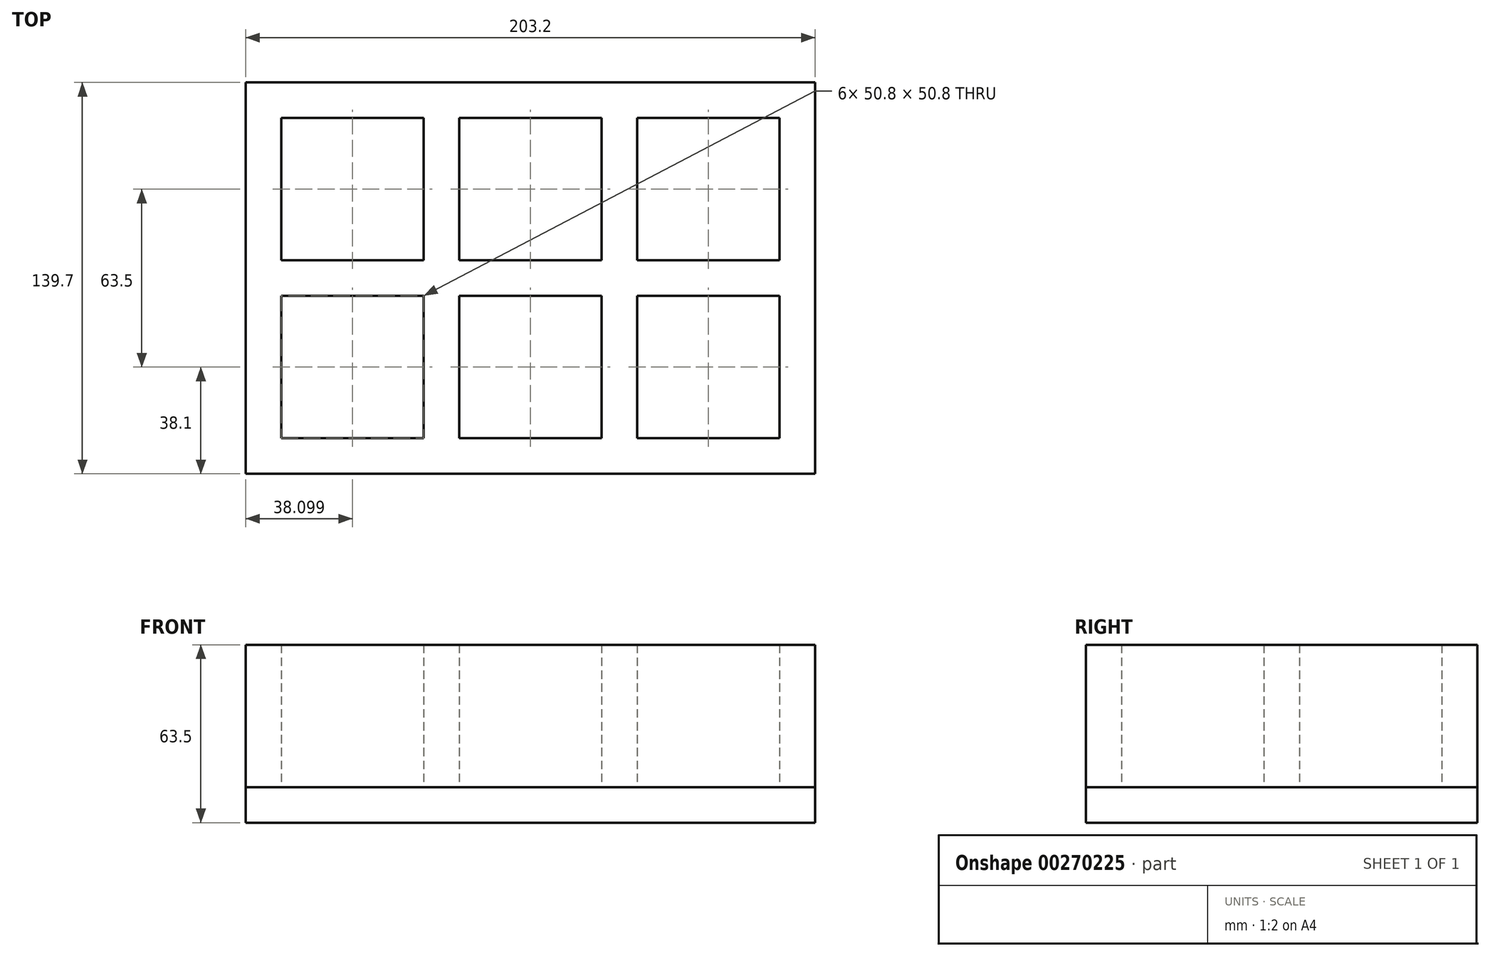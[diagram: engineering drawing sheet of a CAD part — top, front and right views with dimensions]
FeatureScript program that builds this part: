
annotation { "Feature Type Name" : "Feature", "Feature Type Description" : "" }
export const myFeature = defineFeature(function(context is Context, id is Id, definition is map)
    precondition{}
    {
        {
            var Q0;
            Q0=qCreatedBy(makeId("Top.planeOp"),FACE);
            var sketch = newSketch(context, id + "F0", { "sketchPlane" : qUnion([Q0])});
            skLineSegment(sketch, "E0.bottom", {"start": v(-73.54, -55.31) * mm, "end": v(104.26, -55.31) * mm});
            skLineSegment(sketch, "E0.top", {"start": v(-73.54, 58.99) * mm, "end": v(104.26, 58.99) * mm});
            skLineSegment(sketch, "E0.left", {"start": v(-73.54, -55.31) * mm, "end": v(-73.54, 58.99) * mm});
            skLineSegment(sketch, "E0.right", {"start": v(104.26, -55.31) * mm, "end": v(104.26, 58.99) * mm});
            skLineSegment(sketch, "E1", {"start": v(-10.04, 58.99) * mm, "end": v(-10.04, -55.31) * mm});
            skLineSegment(sketch, "E2", {"start": v(53.46, 58.99) * mm, "end": v(53.46, -55.31) * mm});
            skLineSegment(sketch, "E3", {"start": v(-22.74, 58.99) * mm, "end": v(-22.74, -55.31) * mm});
            skLineSegment(sketch, "E4", {"start": v(40.76, 58.99) * mm, "end": v(40.76, -55.31) * mm});
            skLineSegment(sketch, "E5", {"start": v(-73.54, 8.19) * mm, "end": v(104.26, 8.19) * mm});
            skLineSegment(sketch, "E6", {"start": v(-73.54, -4.51) * mm, "end": v(104.26, -4.51) * mm});
            skLineSegment(sketch, "E7.bottom", {"start": v(-86.24, 71.69) * mm, "end": v(116.96, 71.69) * mm});
            skLineSegment(sketch, "E7.top", {"start": v(-86.24, -68.01) * mm, "end": v(116.96, -68.01) * mm});
            skLineSegment(sketch, "E7.left", {"start": v(-86.24, 71.69) * mm, "end": v(-86.24, -68.01) * mm});
            skLineSegment(sketch, "E7.right", {"start": v(116.96, 71.69) * mm, "end": v(116.96, -68.01) * mm});
            skSolve(sketch);
        }
        {
            var Q0;
            Q0=makeQuery(id+"F0.imprint","IMPRINT",FACE,{"disambiguationData":[TD([[makeQuery(id+"F0.imprint","IMPRINT",EDGE,{"derivedFrom":sQuery(id+"F0.wireOp",EDGE,"E7.bottom")}),-1.0]])]});
            var Q1;
            {var subQ0=sQuery(id+"F0.wireOp",EDGE,"E5");var subQ1=sQuery(id+"F0.wireOp",EDGE,"E0.left");var subQ2=makeQuery(id+"F0.imprint","INTERSECT",VERTEX,{"derivedFrom":[subQ1,subQ0]});Q1=makeQuery(id+"F0.imprint","IMPRINT",FACE,{"disambiguationData":[TD([[makeQuery(id+"F0.imprint","IMPRINT",EDGE,{"disambiguationData":[TD([[subQ2,1.0]])],"derivedFrom":subQ1}),-1.0]])]});}
            var Q2;
            {var subQ0=sQuery(id+"F0.wireOp",EDGE,"E5");var subQ1=sQuery(id+"F0.wireOp",EDGE,"E1");var subQ2=makeQuery(id+"F0.imprint","INTERSECT",VERTEX,{"derivedFrom":[subQ1,subQ0]});Q2=makeQuery(id+"F0.imprint","IMPRINT",FACE,{"disambiguationData":[TD([[makeQuery(id+"F0.imprint","IMPRINT",EDGE,{"disambiguationData":[TD([[subQ2,-1.0]])],"derivedFrom":subQ1}),1.0]])]});}
            var Q3;
            {var subQ0=sQuery(id+"F0.wireOp",EDGE,"E5");var subQ1=sQuery(id+"F0.wireOp",EDGE,"E1");var subQ2=makeQuery(id+"F0.imprint","INTERSECT",VERTEX,{"derivedFrom":[subQ1,subQ0]});Q3=makeQuery(id+"F0.imprint","IMPRINT",FACE,{"disambiguationData":[TD([[makeQuery(id+"F0.imprint","IMPRINT",EDGE,{"disambiguationData":[TD([[subQ2,-1.0]])],"derivedFrom":subQ1}),-1.0]])]});}
            var Q4;
            {var subQ0=sQuery(id+"F0.wireOp",EDGE,"E5");var subQ1=sQuery(id+"F0.wireOp",EDGE,"E2");var subQ2=makeQuery(id+"F0.imprint","INTERSECT",VERTEX,{"derivedFrom":[subQ1,subQ0]});Q4=makeQuery(id+"F0.imprint","IMPRINT",FACE,{"disambiguationData":[TD([[makeQuery(id+"F0.imprint","IMPRINT",EDGE,{"disambiguationData":[TD([[subQ2,-1.0]])],"derivedFrom":subQ1}),-1.0]])]});}
            var Q5;
            {var subQ0=sQuery(id+"F0.wireOp",EDGE,"E5");var subQ1=sQuery(id+"F0.wireOp",EDGE,"E0.right");var subQ2=makeQuery(id+"F0.imprint","INTERSECT",VERTEX,{"derivedFrom":[subQ1,subQ0]});Q5=makeQuery(id+"F0.imprint","IMPRINT",FACE,{"disambiguationData":[TD([[makeQuery(id+"F0.imprint","IMPRINT",EDGE,{"disambiguationData":[TD([[subQ2,1.0]])],"derivedFrom":subQ1}),1.0]])]});}
            var Q6;
            {var subQ0=sQuery(id+"F0.wireOp",EDGE,"E2");var subQ1=sQuery(id+"F0.wireOp",EDGE,"E0.bottom");var subQ2=makeQuery(id+"F0.imprint","INTERSECT",VERTEX,{"derivedFrom":[subQ1,subQ0]});Q6=makeQuery(id+"F0.imprint","IMPRINT",FACE,{"disambiguationData":[TD([[makeQuery(id+"F0.imprint","IMPRINT",EDGE,{"disambiguationData":[TD([[subQ2,1.0]])],"derivedFrom":subQ1}),1.0]])]});}
            var Q7;
            {var subQ0=sQuery(id+"F0.wireOp",EDGE,"E1");var subQ1=sQuery(id+"F0.wireOp",EDGE,"E0.bottom");var subQ2=makeQuery(id+"F0.imprint","INTERSECT",VERTEX,{"derivedFrom":[subQ1,subQ0]});Q7=makeQuery(id+"F0.imprint","IMPRINT",FACE,{"disambiguationData":[TD([[makeQuery(id+"F0.imprint","IMPRINT",EDGE,{"disambiguationData":[TD([[subQ2,1.0]])],"derivedFrom":subQ1}),1.0]])]});}
            var Q8;
            {var subQ0=sQuery(id+"F0.wireOp",EDGE,"E2");var subQ1=sQuery(id+"F0.wireOp",EDGE,"E0.top");var subQ2=makeQuery(id+"F0.imprint","INTERSECT",VERTEX,{"derivedFrom":[subQ1,subQ0]});Q8=makeQuery(id+"F0.imprint","IMPRINT",FACE,{"disambiguationData":[TD([[makeQuery(id+"F0.imprint","IMPRINT",EDGE,{"disambiguationData":[TD([[subQ2,1.0]])],"derivedFrom":subQ1}),-1.0]])]});}
            var Q9;
            {var subQ0=sQuery(id+"F0.wireOp",EDGE,"E1");var subQ1=sQuery(id+"F0.wireOp",EDGE,"E0.top");var subQ2=makeQuery(id+"F0.imprint","INTERSECT",VERTEX,{"derivedFrom":[subQ1,subQ0]});Q9=makeQuery(id+"F0.imprint","IMPRINT",FACE,{"disambiguationData":[TD([[makeQuery(id+"F0.imprint","IMPRINT",EDGE,{"disambiguationData":[TD([[subQ2,1.0]])],"derivedFrom":subQ1}),-1.0]])]});}
            extrude(context, id + "F1", {"entities" : qUnion([Q0, Q1, Q2, Q3, Q4, Q5, Q6, Q7, Q8, Q9]), "depth" : 50.8 * mm});
        }
        {
            var Q0;
            {var subQ0=sQuery(id+"F0.wireOp",EDGE,"E0.right");var subQ1=sQuery(id+"F0.wireOp",EDGE,"E0.top");var subQ2=makeQuery(id+"F0.imprint","INTERSECT",VERTEX,{"derivedFrom":[subQ1,subQ0]});Q0=makeQuery(id+"F0.imprint","IMPRINT",FACE,{"disambiguationData":[TD([[makeQuery(id+"F0.imprint","IMPRINT",EDGE,{"disambiguationData":[TD([[subQ2,1.0]])],"derivedFrom":subQ1}),-1.0]])]});}
            var Q1;
            {var subQ0=sQuery(id+"F0.wireOp",EDGE,"E5");var subQ1=sQuery(id+"F0.wireOp",EDGE,"E0.right");var subQ2=makeQuery(id+"F0.imprint","INTERSECT",VERTEX,{"derivedFrom":[subQ1,subQ0]});Q1=makeQuery(id+"F0.imprint","IMPRINT",FACE,{"disambiguationData":[TD([[makeQuery(id+"F0.imprint","IMPRINT",EDGE,{"disambiguationData":[TD([[subQ2,1.0]])],"derivedFrom":subQ1}),1.0]])]});}
            var Q2;
            {var subQ0=sQuery(id+"F0.wireOp",EDGE,"E0.right");var subQ1=sQuery(id+"F0.wireOp",EDGE,"E0.bottom");var subQ2=makeQuery(id+"F0.imprint","INTERSECT",VERTEX,{"derivedFrom":[subQ1,subQ0]});Q2=makeQuery(id+"F0.imprint","IMPRINT",FACE,{"disambiguationData":[TD([[makeQuery(id+"F0.imprint","IMPRINT",EDGE,{"disambiguationData":[TD([[subQ2,1.0]])],"derivedFrom":subQ1}),1.0]])]});}
            var Q3;
            {var subQ0=sQuery(id+"F0.wireOp",EDGE,"E1");var subQ1=sQuery(id+"F0.wireOp",EDGE,"E0.top");var subQ2=makeQuery(id+"F0.imprint","INTERSECT",VERTEX,{"derivedFrom":[subQ1,subQ0]});Q3=makeQuery(id+"F0.imprint","IMPRINT",FACE,{"disambiguationData":[TD([[makeQuery(id+"F0.imprint","IMPRINT",EDGE,{"disambiguationData":[TD([[subQ2,-1.0]])],"derivedFrom":subQ1}),-1.0]])]});}
            var Q4;
            {var subQ0=sQuery(id+"F0.wireOp",EDGE,"E2");var subQ1=sQuery(id+"F0.wireOp",EDGE,"E0.top");var subQ2=makeQuery(id+"F0.imprint","INTERSECT",VERTEX,{"derivedFrom":[subQ1,subQ0]});Q4=makeQuery(id+"F0.imprint","IMPRINT",FACE,{"disambiguationData":[TD([[makeQuery(id+"F0.imprint","IMPRINT",EDGE,{"disambiguationData":[TD([[subQ2,1.0]])],"derivedFrom":subQ1}),-1.0]])]});}
            var Q5;
            {var subQ0=sQuery(id+"F0.wireOp",EDGE,"E5");var subQ1=sQuery(id+"F0.wireOp",EDGE,"E2");var subQ2=makeQuery(id+"F0.imprint","INTERSECT",VERTEX,{"derivedFrom":[subQ1,subQ0]});Q5=makeQuery(id+"F0.imprint","IMPRINT",FACE,{"disambiguationData":[TD([[makeQuery(id+"F0.imprint","IMPRINT",EDGE,{"disambiguationData":[TD([[subQ2,-1.0]])],"derivedFrom":subQ1}),-1.0]])]});}
            var Q6;
            {var subQ0=sQuery(id+"F0.wireOp",EDGE,"E5");var subQ1=sQuery(id+"F0.wireOp",EDGE,"E1");var subQ2=makeQuery(id+"F0.imprint","INTERSECT",VERTEX,{"derivedFrom":[subQ1,subQ0]});Q6=makeQuery(id+"F0.imprint","IMPRINT",FACE,{"disambiguationData":[TD([[makeQuery(id+"F0.imprint","IMPRINT",EDGE,{"disambiguationData":[TD([[subQ2,-1.0]])],"derivedFrom":subQ1}),1.0]])]});}
            var Q7;
            {var subQ0=sQuery(id+"F0.wireOp",EDGE,"E5");var subQ1=sQuery(id+"F0.wireOp",EDGE,"E0.left");var subQ2=makeQuery(id+"F0.imprint","INTERSECT",VERTEX,{"derivedFrom":[subQ1,subQ0]});Q7=makeQuery(id+"F0.imprint","IMPRINT",FACE,{"disambiguationData":[TD([[makeQuery(id+"F0.imprint","IMPRINT",EDGE,{"disambiguationData":[TD([[subQ2,1.0]])],"derivedFrom":subQ1}),-1.0]])]});}
            var Q8;
            {var subQ0=sQuery(id+"F0.wireOp",EDGE,"E5");var subQ1=sQuery(id+"F0.wireOp",EDGE,"E1");var subQ2=makeQuery(id+"F0.imprint","INTERSECT",VERTEX,{"derivedFrom":[subQ1,subQ0]});Q8=makeQuery(id+"F0.imprint","IMPRINT",FACE,{"disambiguationData":[TD([[makeQuery(id+"F0.imprint","IMPRINT",EDGE,{"disambiguationData":[TD([[subQ2,-1.0]])],"derivedFrom":subQ1}),-1.0]])]});}
            var Q9;
            {var subQ0=sQuery(id+"F0.wireOp",EDGE,"E1");var subQ1=sQuery(id+"F0.wireOp",EDGE,"E0.top");var subQ2=makeQuery(id+"F0.imprint","INTERSECT",VERTEX,{"derivedFrom":[subQ1,subQ0]});Q9=makeQuery(id+"F0.imprint","IMPRINT",FACE,{"disambiguationData":[TD([[makeQuery(id+"F0.imprint","IMPRINT",EDGE,{"disambiguationData":[TD([[subQ2,1.0]])],"derivedFrom":subQ1}),-1.0]])]});}
            var Q10;
            {var subQ0=sQuery(id+"F0.wireOp",EDGE,"E0.left");var subQ1=sQuery(id+"F0.wireOp",EDGE,"E0.top");var subQ2=makeQuery(id+"F0.imprint","INTERSECT",VERTEX,{"derivedFrom":[subQ1,subQ0]});Q10=makeQuery(id+"F0.imprint","IMPRINT",FACE,{"disambiguationData":[TD([[makeQuery(id+"F0.imprint","IMPRINT",EDGE,{"disambiguationData":[TD([[subQ2,-1.0]])],"derivedFrom":subQ1}),-1.0]])]});}
            var Q11;
            {var subQ0=sQuery(id+"F0.wireOp",EDGE,"E2");var subQ1=sQuery(id+"F0.wireOp",EDGE,"E0.bottom");var subQ2=makeQuery(id+"F0.imprint","INTERSECT",VERTEX,{"derivedFrom":[subQ1,subQ0]});Q11=makeQuery(id+"F0.imprint","IMPRINT",FACE,{"disambiguationData":[TD([[makeQuery(id+"F0.imprint","IMPRINT",EDGE,{"disambiguationData":[TD([[subQ2,1.0]])],"derivedFrom":subQ1}),1.0]])]});}
            var Q12;
            {var subQ0=sQuery(id+"F0.wireOp",EDGE,"E1");var subQ1=sQuery(id+"F0.wireOp",EDGE,"E0.bottom");var subQ2=makeQuery(id+"F0.imprint","INTERSECT",VERTEX,{"derivedFrom":[subQ1,subQ0]});Q12=makeQuery(id+"F0.imprint","IMPRINT",FACE,{"disambiguationData":[TD([[makeQuery(id+"F0.imprint","IMPRINT",EDGE,{"disambiguationData":[TD([[subQ2,-1.0]])],"derivedFrom":subQ1}),1.0]])]});}
            var Q13;
            {var subQ0=sQuery(id+"F0.wireOp",EDGE,"E1");var subQ1=sQuery(id+"F0.wireOp",EDGE,"E0.bottom");var subQ2=makeQuery(id+"F0.imprint","INTERSECT",VERTEX,{"derivedFrom":[subQ1,subQ0]});Q13=makeQuery(id+"F0.imprint","IMPRINT",FACE,{"disambiguationData":[TD([[makeQuery(id+"F0.imprint","IMPRINT",EDGE,{"disambiguationData":[TD([[subQ2,1.0]])],"derivedFrom":subQ1}),1.0]])]});}
            var Q14;
            {var subQ0=sQuery(id+"F0.wireOp",EDGE,"E0.left");var subQ1=sQuery(id+"F0.wireOp",EDGE,"E0.bottom");var subQ2=makeQuery(id+"F0.imprint","INTERSECT",VERTEX,{"derivedFrom":[subQ1,subQ0]});Q14=makeQuery(id+"F0.imprint","IMPRINT",FACE,{"disambiguationData":[TD([[makeQuery(id+"F0.imprint","IMPRINT",EDGE,{"disambiguationData":[TD([[subQ2,-1.0]])],"derivedFrom":subQ1}),1.0]])]});}
            var Q15;
            Q15=makeQuery(id+"F0.imprint","IMPRINT",FACE,{"disambiguationData":[TD([[makeQuery(id+"F0.imprint","IMPRINT",EDGE,{"derivedFrom":sQuery(id+"F0.wireOp",EDGE,"E7.bottom")}),-1.0]])]});
            extrude(context, id + "F2", {"entities" : qUnion([Q0, Q1, Q2, Q3, Q4, Q5, Q6, Q7, Q8, Q9, Q10, Q11, Q12, Q13, Q14, Q15]), "oppositeDirection" : true, "depth" : 12.7 * mm});
        }
    });
